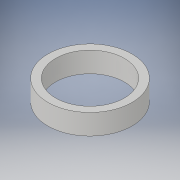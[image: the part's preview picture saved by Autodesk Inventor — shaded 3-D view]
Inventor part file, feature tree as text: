
AUTODESK INVENTOR PART (.ipt)
format: ipt  version: 2017 (Build 210142000, 142)  size: 97,280 bytes
history: native  units: in
note: dims shown in document units (in); Inventor stores cm internally (conversion verified against a paired STEP export)
features: extrude x1, sketch x1
ambient origin geometry x8: Origin, YZ Plane, XZ Plane, XY Plane, X Axis, Y Axis, Z Axis, Center Point
bodies: Solid1 (feature_tree)
feature tree (2):
  extrude  "Extrusion1"  Depth=0.74in
  sketch  "Sketch1"  dims[d0=2.49in d1=3.04in d2=0.74in d3=0.0in]
